# Revit family: 11-TRIMBOARD-AND-STEALTH-TRIM-CADS-117-8-standard-st-4-REVIT_Versatex-Profile-5-4in-x-8in-STEALTH-TRIM--75in-Pocket
name_source: partatom
category: Profiles
units: mm (PartAtom-declared; Revit-internal decimal feet)

## family parameters
Profile Usage = <Generic>
Rotate with component = No
Section Shape = Not Defined

## types (1)
- 11-TRIMBOARD-AND-STEALTH-TRIM-CADS-117-8-standard-st-4-REVIT_Versatex-Profile-5-4in-x-8in-STEALTH-TRIM--75in-Pocket
    Description = NOMINAL 5/4" X 8" STEALTH TRIM
    Literature = https://versatex.com
    Manufacturer = Versatex
    Manufacturer Fax = 724-857-1171
    Manufacturer Website = https://versatex.com
    Message Manufacturer = https://versatex.com
    Model = STBSM/TR540818
    Pocket Depth = 0' - 0 3/4"
    Sales Information = https://versatex.com
    Specification = https://www.arcat.com
    URL = https://versatex.com
    Warranty = https://versatex.com

## geometry (parser evidence)
native form markers: Blend x2
no freeform markers — native parametric forms only
